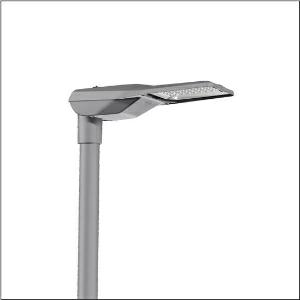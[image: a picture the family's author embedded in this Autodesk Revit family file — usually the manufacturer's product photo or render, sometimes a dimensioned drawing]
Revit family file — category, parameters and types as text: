
# Revit family: streetlight_sl_21_mini___p0_8a_5xe2u33s08jb_688f
name_source: partatom
category: Lighting Fixtures
units: mm (PartAtom-declared; Revit-internal decimal feet)

## family parameters
Cut with Voids When Loaded = No
Host = Face
Light Source = No
Part Type = Normal
Room Calculation Point = No
Round Connector Dimension = Use Diameter
Shared = No

## types (1)
- --- (1 x LED, 13050 lm, 88.6 W, 3000K)
    Apparent Load = 89 VA
    CIE Flux Codes = 36 69 97 100 100
    Color Rendering = 70
    Color Temperature = 3000K
    Default Elevation = 1800 mm
    Description = Streetlight SL 21 mini, mast luminaire, primary light control with lens, of PMMA, primary optical cover: cover, of toughened safety glass, transparent, light distribution: P0.8a, light emission: direct distribution, primary light characteristic: asymmetric, installation type: post-top, side-entry, LED, High Power LED, rated luminous flux: 13.050lm, luminous efficacy: 147lm/W, light colour: 730, colour temperature: 3000K, control gear: D4i, control: pre-setting: logarithmic dimming characteristic, flexible luminous flux parameterisation, time-dependent luminous flux control, constant luminous flux control, overheat protection, mains connection: 220..240V, AC, 50/60Hz, start of lifetime: 89W, end of service life: 92W, reduction: 41W, luminaire housing, of diecast aluminium, powder-coated, SITECO metallic grey (DB 702S), corrosivity category C5 high according to DIN EN ISO 12944, multi-level sealing system, sealing non-destructively replaceable, inclination adjustable: 0°, 5°, 10°, 15°, please order mast flange separately, length: 628mm, width: 235mm, height: 110mm, mast flange for spigot size: 42mm (side-entry): 5XC10008XM4, 60/48mm (side-entry/post-top): 5XC10108XM2, 76/60mm (side-entry/post-top): 5XC10108XM1, mounting height: 4..8m, Smart Interface above, protection rating (complete): IP66, insulation class (complete): insulation class II (safety insulation), certification: CE, ENEC, ENEC+, VDE, impact resistance: IK10, permissible operating ambient temperature for outdoor applications: -40..+50°C, standard-compliant lighting for roads and squares, packaging unit: 1 piece

Light Distribution: P0.8a
    Height = 110 mm
    Lamp = 1 x LED
    Lamp Light Flux = 13050 lm
    Lamp Power = 88.6 W
    Lamp count = 1
    Length = 625 mm
    Luminous efficacy = 147 lm/W
    Manufacturer = Siteco
    ModVariant = No
    Model = 5XE2U33S08JB
    Mounting Place = Pole
    Mounting Type = Pole top
    Number of Poles = 1
    OnlyDefault = Yes
    Power Factor = 1
    Product Name = Streetlight SL 21 mini | P0.8a
    Product group = mast luminaire | pylon top
    ProductGroupID = 6100
    Protection Class = Protection class II
    Protection Degree = IP 66
    RLX_Detail_Level = 1
    RLX_Emergency_Light_Flux = 0 lm
    RLX_Emergency_Type = 0
    RLX_Emergency_Type_DB = No
    RlxData = <blob elided: 26065 chars, md5=e6893e49>
    Socket = socket
    Standby Power = 0 W
    System Light Flux = 13050 lm
    System Power = 89 W
    Type Comments = factory setting: luminous flux: 100 % | dim-lin: 254 | 915 mA
    Type Image = l_1003515.jpg
    URL = http://relux.com
    VarID = @adj_034639
    Voltage = 0 V
    Weight = 0.00 kg
    Width = 234 mm

## geometry (parser evidence)
native form markers: Blend x4, Sweep x11
no freeform markers — native parametric forms only
